# Revit family: COFFRET ELEC HOSPIVAC G EVISA
name_source: partatom
category: Equipement de génie climatique
revit_build: Autodesk Revit 2018 (Build: 20170223_1515(x64)
units: mm (PartAtom-declared; Revit-internal decimal feet)

## family parameters
Basée sur le plan de construction = Non
Classification = Aucun
Cote de connecteur circulaire = Utiliser le diamètre
Couper avec des vides une fois chargée = Non
Partagée = Non
Point de calcul de pièce = Non
Toujours verticalement = Oui
Type d'élément = Normal

## types (33) — shared parameters
BRANCHEMENT_TERRE = Oui
COS_PHI = 0.9
DOUBLE_ALIMENTATION = Oui
EMBASE_IG = 60 mm  [stored 0.19685 ft]
HAUTEUR = 344 mm
HAUT_PE = 22.5 mm  [stored 0.0738189 ft]
HAUT_PM2 = 195 mm  [stored 0.639764 ft]
LONGUEUR = 600 mm  [stored 1.9685 ft]
LONG_COFF = 600 mm  [stored 1.9685 ft]
NBR_POLES = 3
NEUTRE = Oui
PROF_IG = 44 mm  [stored 0.144357 ft]
TENSION_ALIM = 400 V
ZONE_MAINTENANCE = Oui
ØDEPART = 20 mm  [stored 0.0656168 ft]
ØFIX = 12 mm  [stored 0.0393701 ft]
ØPE = 40 mm
zero-valued in all types: POIDS(Kg)

## per-type parameters (varying)
- COFFRET PM2 HOSPIVAC G2 E025.R: DESCR_ALIM_MOT=Puissance moteur ; 4G2.5mm²; DESCR_ALIM_MOT_3=Ne pas utiliser; DESCR_ALIM_MOT_4=Ne pas utiliser; DESCR_ALIM_X=Alimentation X ; 5G2.5mm²; DESCR_ALIM_Y=Alimentation Y ; 5G2.5mm²; ENTRAXE_IG=425 mm  [stored 1.39436 ft]; ENTRAXE_PE=526 mm  [stored 1.72572 ft]; HAUT_COFF=300 mm  [stored 0.984252 ft]; HAUT_FIX=258 mm; LARGEUR=300 mm  [stored 0.984252 ft]; LARG_COFF=300 mm  [stored 0.984252 ft]; LONG_FIX=558 mm; OFFSET_HAUT_IG=107.5 mm; OFFSET_HAUT_PM2=135 mm; OFFSET_LARG_PE=80 mm  [stored 0.262467 ft]; PROTECTION_AMONT_X=Disjoncteur courbe D 10A; PROTECTION_AMONT_Y=Disjoncteur courbe D 10A; PUISS_APPARENTE=833 VA; PUISS_APPARENTE_2=833 VA; PUISS_APPARENTE_MOT=833 VA; PUISS_APPARENTE_MOT_3=0 VA; PUISS_APPARENTE_MOT_4=0 VA; PUISS_ELECT=1 kW; PUISS_ELECT_2=1 kW; PUISS_MOT=1 kW; PUISS_MOT_3=0 kW; PUISS_MOT_4=0 kW
- COFFRET PM2 HOSPIVAC G2 E040.R: DESCR_ALIM_MOT=Puissance moteur ; 4G2.5mm²; DESCR_ALIM_MOT_3=Ne pas utiliser; DESCR_ALIM_MOT_4=Ne pas utiliser; DESCR_ALIM_X=Alimentation X ; 5G2.5mm²; DESCR_ALIM_Y=Alimentation Y ; 5G2.5mm²; ENTRAXE_IG=425 mm  [stored 1.39436 ft]; ENTRAXE_PE=526 mm  [stored 1.72572 ft]; HAUT_COFF=300 mm  [stored 0.984252 ft]; HAUT_FIX=258 mm; LARGEUR=300 mm  [stored 0.984252 ft]; LARG_COFF=300 mm  [stored 0.984252 ft]; LONG_FIX=558 mm; OFFSET_HAUT_IG=107.5 mm; OFFSET_HAUT_PM2=135 mm; OFFSET_LARG_PE=80 mm  [stored 0.262467 ft]; PROTECTION_AMONT_X=Disjoncteur courbe D 10A; PROTECTION_AMONT_Y=Disjoncteur courbe D 10A; PUISS_APPARENTE=1222 VA; PUISS_APPARENTE_2=1222 VA; PUISS_APPARENTE_MOT=1222 VA; PUISS_APPARENTE_MOT_3=0 VA; PUISS_APPARENTE_MOT_4=0 VA; PUISS_ELECT=1 kW; PUISS_ELECT_2=1 kW; PUISS_MOT=1 kW; PUISS_MOT_3=0 kW; PUISS_MOT_4=0 kW
- COFFRET PM2 HOSPIVAC G2 E065.R: DESCR_ALIM_MOT=Puissance moteur ; 4G2.5mm²; DESCR_ALIM_MOT_3=Ne pas utiliser; DESCR_ALIM_MOT_4=Ne pas utiliser; DESCR_ALIM_X=Alimentation X ; 5G2.5mm²; DESCR_ALIM_Y=Alimentation Y ; 5G2.5mm²; ENTRAXE_IG=425 mm  [stored 1.39436 ft]; ENTRAXE_PE=526 mm  [stored 1.72572 ft]; HAUT_COFF=300 mm  [stored 0.984252 ft]; HAUT_FIX=258 mm; LARGEUR=300 mm  [stored 0.984252 ft]; LARG_COFF=300 mm  [stored 0.984252 ft]; LONG_FIX=558 mm; OFFSET_HAUT_IG=107.5 mm; OFFSET_HAUT_PM2=135 mm; OFFSET_LARG_PE=80 mm  [stored 0.262467 ft]; PROTECTION_AMONT_X=Disjoncteur courbe D 10A; PROTECTION_AMONT_Y=Disjoncteur courbe D 10A; PUISS_APPARENTE=1667 VA; PUISS_APPARENTE_2=1667 VA; PUISS_APPARENTE_MOT=1667 VA; PUISS_APPARENTE_MOT_3=0 VA; PUISS_APPARENTE_MOT_4=0 VA; PUISS_ELECT=2 kW; PUISS_ELECT_2=2 kW; PUISS_MOT=2 kW; PUISS_MOT_3=0 kW; PUISS_MOT_4=0 kW
- COFFRET PM2 HOSPIVAC G3 E025.R: DESCR_ALIM_MOT=Puissance moteur ; 4G2.5mm²; DESCR_ALIM_MOT_3=Puissance moteur ; 4G2.5mm²; DESCR_ALIM_MOT_4=Ne pas utiliser; DESCR_ALIM_X=Alimentation X ; 5G2.5mm²; DESCR_ALIM_Y=Alimentation Y ; 5G2.5mm²; ENTRAXE_IG=425 mm  [stored 1.39436 ft]; ENTRAXE_PE=526 mm  [stored 1.72572 ft]; HAUT_COFF=300 mm  [stored 0.984252 ft]; HAUT_FIX=258 mm; LARGEUR=300 mm  [stored 0.984252 ft]; LARG_COFF=300 mm  [stored 0.984252 ft]; LONG_FIX=558 mm; OFFSET_HAUT_IG=107.5 mm; OFFSET_HAUT_PM2=135 mm; OFFSET_LARG_PE=80 mm  [stored 0.262467 ft]; PROTECTION_AMONT_X=Disjoncteur courbe D 6A; PROTECTION_AMONT_Y=Disjoncteur courbe D 10A; PUISS_APPARENTE=833 VA; PUISS_APPARENTE_2=1667 VA; PUISS_APPARENTE_MOT=833 VA; PUISS_APPARENTE_MOT_3=833 VA; PUISS_APPARENTE_MOT_4=0 VA; PUISS_ELECT=1 kW; PUISS_ELECT_2=2 kW; PUISS_MOT=1 kW; PUISS_MOT_3=1 kW; PUISS_MOT_4=0 kW
- COFFRET PM2 HOSPIVAC G3 E040.R: DESCR_ALIM_MOT=Puissance moteur ; 4G2.5mm²; DESCR_ALIM_MOT_3=Puissance moteur ; 4G2.5mm²; DESCR_ALIM_MOT_4=Ne pas utiliser; DESCR_ALIM_X=Alimentation X ; 5G2.5mm²; DESCR_ALIM_Y=Alimentation Y ; 5G2.5mm²; ENTRAXE_IG=425 mm  [stored 1.39436 ft]; ENTRAXE_PE=526 mm  [stored 1.72572 ft]; HAUT_COFF=300 mm  [stored 0.984252 ft]; HAUT_FIX=258 mm; LARGEUR=300 mm  [stored 0.984252 ft]; LARG_COFF=300 mm  [stored 0.984252 ft]; LONG_FIX=558 mm; OFFSET_HAUT_IG=107.5 mm; OFFSET_HAUT_PM2=135 mm; OFFSET_LARG_PE=80 mm  [stored 0.262467 ft]; PROTECTION_AMONT_X=Disjoncteur courbe D 6A; PROTECTION_AMONT_Y=Disjoncteur courbe D 10A; PUISS_APPARENTE=1222 VA; PUISS_APPARENTE_2=2444 VA; PUISS_APPARENTE_MOT=1222 VA; PUISS_APPARENTE_MOT_3=1222 VA; PUISS_APPARENTE_MOT_4=0 VA; PUISS_ELECT=1 kW; PUISS_ELECT_2=2 kW; PUISS_MOT=1 kW; PUISS_MOT_3=1 kW; PUISS_MOT_4=0 kW
- COFFRET PM2 HOSPIVAC G3 E065.R: DESCR_ALIM_MOT=Puissance moteur ; 4G2.5mm²; DESCR_ALIM_MOT_3=Puissance moteur ; 4G2.5mm²; DESCR_ALIM_MOT_4=Ne pas utiliser; DESCR_ALIM_X=Alimentation X ; 5G2.5mm²; DESCR_ALIM_Y=Alimentation Y ; 5G2.5mm²; ENTRAXE_IG=425 mm  [stored 1.39436 ft]; ENTRAXE_PE=526 mm  [stored 1.72572 ft]; HAUT_COFF=300 mm  [stored 0.984252 ft]; HAUT_FIX=258 mm; LARGEUR=300 mm  [stored 0.984252 ft]; LARG_COFF=300 mm  [stored 0.984252 ft]; LONG_FIX=558 mm; OFFSET_HAUT_IG=107.5 mm; OFFSET_HAUT_PM2=135 mm; OFFSET_LARG_PE=80 mm  [stored 0.262467 ft]; PROTECTION_AMONT_X=Disjoncteur courbe D 6A; PROTECTION_AMONT_Y=Disjoncteur courbe D 16A; PUISS_APPARENTE=1667 VA; PUISS_APPARENTE_2=3333 VA; PUISS_APPARENTE_MOT=1667 VA; PUISS_APPARENTE_MOT_3=1667 VA; PUISS_APPARENTE_MOT_4=0 VA; PUISS_ELECT=2 kW; PUISS_ELECT_2=3 kW; PUISS_MOT=2 kW; PUISS_MOT_3=2 kW; PUISS_MOT_4=0 kW
- COFFRET PM2 HOSPIVAC G4 E100.R: DESCR_ALIM_MOT=Puissance moteur ; 4G2.5mm²; DESCR_ALIM_MOT_3=Puissance moteur ; 4G2.5mm²; DESCR_ALIM_MOT_4=Puissance moteur ; 4G2.5mm²; DESCR_ALIM_X=Alimentation X ; 5G2.5mm²; DESCR_ALIM_Y=Alimentation Y ; 5G2.5mm²; ENTRAXE_IG=180 mm  [stored 0.590551 ft]; ENTRAXE_PE=420 mm  [stored 1.37795 ft]; HAUT_COFF=800 mm  [stored 2.62467 ft]; HAUT_FIX=755 mm  [stored 2.47703 ft]; LARGEUR=250 mm  [stored 0.82021 ft]; LARG_COFF=250 mm  [stored 0.82021 ft]; LONG_FIX=555 mm  [stored 1.82087 ft]; OFFSET_HAUT_IG=165 mm; OFFSET_HAUT_PM2=320 mm  [stored 1.04987 ft]; OFFSET_LARG_PE=185 mm  [stored 0.606955 ft]; PROTECTION_AMONT_X=Disjoncteur courbe D 16A; PROTECTION_AMONT_Y=Disjoncteur courbe D 16A; PUISS_APPARENTE=4889 VA; PUISS_APPARENTE_2=4889 VA; PUISS_APPARENTE_MOT=2444 VA; PUISS_APPARENTE_MOT_3=2444 VA; PUISS_APPARENTE_MOT_4=2444 VA; PUISS_ELECT=4 kW; PUISS_ELECT_2=4 kW; PUISS_MOT=2 kW; PUISS_MOT_3=2 kW; PUISS_MOT_4=2 kW
- COFFRET PM2 HOSPIVAC G4 E150.R: DESCR_ALIM_MOT=Puissance moteur ; 4G2.5mm²; DESCR_ALIM_MOT_3=Puissance moteur ; 4G2.5mm²; DESCR_ALIM_MOT_4=Puissance moteur ; 4G2.5mm²; DESCR_ALIM_X=Alimentation X ; 5G4mm²; DESCR_ALIM_Y=Alimentation Y ; 5G4mm²; ENTRAXE_IG=180 mm  [stored 0.590551 ft]; ENTRAXE_PE=420 mm  [stored 1.37795 ft]; HAUT_COFF=800 mm  [stored 2.62467 ft]; HAUT_FIX=755 mm  [stored 2.47703 ft]; LARGEUR=250 mm  [stored 0.82021 ft]; LARG_COFF=250 mm  [stored 0.82021 ft]; LONG_FIX=555 mm  [stored 1.82087 ft]; OFFSET_HAUT_IG=165 mm; OFFSET_HAUT_PM2=320 mm  [stored 1.04987 ft]; OFFSET_LARG_PE=185 mm  [stored 0.606955 ft]; PROTECTION_AMONT_X=Disjoncteur courbe D 20A; PROTECTION_AMONT_Y=Disjoncteur courbe D 20A; PUISS_APPARENTE=6667 VA; PUISS_APPARENTE_2=6667 VA; PUISS_APPARENTE_MOT=3333 VA; PUISS_APPARENTE_MOT_3=3333 VA; PUISS_APPARENTE_MOT_4=3333 VA; PUISS_ELECT=6 kW; PUISS_ELECT_2=6 kW; PUISS_MOT=3 kW; PUISS_MOT_3=3 kW; PUISS_MOT_4=3 kW
- COFFRET PM2 HOSPIVAC G4 E300.R: DESCR_ALIM_MOT=Puissance moteur ; 4G2.5mm²; DESCR_ALIM_MOT_3=Puissance moteur ; 4G2.5mm²; DESCR_ALIM_MOT_4=Puissance moteur ; 4G2.5mm²; DESCR_ALIM_X=Alimentation X ; 5G10mm²; DESCR_ALIM_Y=Alimentation Y ; 5G10mm²; ENTRAXE_IG=180 mm  [stored 0.590551 ft]; ENTRAXE_PE=420 mm  [stored 1.37795 ft]; HAUT_COFF=800 mm  [stored 2.62467 ft]; HAUT_FIX=755 mm  [stored 2.47703 ft]; LARGEUR=250 mm  [stored 0.82021 ft]; LARG_COFF=250 mm  [stored 0.82021 ft]; LONG_FIX=555 mm  [stored 1.82087 ft]; OFFSET_HAUT_IG=165 mm; OFFSET_HAUT_PM2=320 mm  [stored 1.04987 ft]; OFFSET_LARG_PE=185 mm  [stored 0.606955 ft]; PROTECTION_AMONT_X=Disjoncteur courbe D 32A; PROTECTION_AMONT_Y=Disjoncteur courbe D 32A; PUISS_APPARENTE=12222 VA; PUISS_APPARENTE_2=12222 VA; PUISS_APPARENTE_MOT=6111 VA; PUISS_APPARENTE_MOT_3=6111 VA; PUISS_APPARENTE_MOT_4=6111 VA; PUISS_ELECT=11 kW; PUISS_ELECT_2=11 kW; PUISS_MOT=6 kW; PUISS_MOT_3=6 kW; PUISS_MOT_4=6 kW
- COFFRET PM2 HOSPIVAC G2 E100.R: DESCR_ALIM_MOT=Puissance moteur ; 4G2.5mm²; DESCR_ALIM_MOT_3=Ne pas utiliser; DESCR_ALIM_MOT_4=Ne pas utiliser; DESCR_ALIM_X=Alimentation X ; 5G2.5mm²; DESCR_ALIM_Y=Alimentation Y ; 5G2.5mm²; ENTRAXE_IG=425 mm  [stored 1.39436 ft]; ENTRAXE_PE=526 mm  [stored 1.72572 ft]; HAUT_COFF=300 mm  [stored 0.984252 ft]; HAUT_FIX=258 mm; LARGEUR=300 mm  [stored 0.984252 ft]; LARG_COFF=300 mm  [stored 0.984252 ft]; LONG_FIX=558 mm; OFFSET_HAUT_IG=107.5 mm; OFFSET_HAUT_PM2=135 mm; OFFSET_LARG_PE=80 mm  [stored 0.262467 ft]; PROTECTION_AMONT_X=Disjoncteur courbe D 10A; PROTECTION_AMONT_Y=Disjoncteur courbe D 10A; PUISS_APPARENTE=2444 VA; PUISS_APPARENTE_2=2444 VA; PUISS_APPARENTE_MOT=2444 VA; PUISS_APPARENTE_MOT_3=0 VA; PUISS_APPARENTE_MOT_4=0 VA; PUISS_ELECT=2 kW; PUISS_ELECT_2=2 kW; PUISS_MOT=2 kW; PUISS_MOT_3=0 kW; PUISS_MOT_4=0 kW
- COFFRET PM2 HOSPIVAC G2 E150.R: DESCR_ALIM_MOT=Puissance moteur ; 4G2.5mm²; DESCR_ALIM_MOT_3=Ne pas utiliser; DESCR_ALIM_MOT_4=Ne pas utiliser; DESCR_ALIM_X=Alimentation X ; 5G2.5mm²; DESCR_ALIM_Y=Alimentation Y ; 5G2.5mm²; ENTRAXE_IG=425 mm  [stored 1.39436 ft]; ENTRAXE_PE=526 mm  [stored 1.72572 ft]; HAUT_COFF=300 mm  [stored 0.984252 ft]; HAUT_FIX=258 mm; LARGEUR=300 mm  [stored 0.984252 ft]; LARG_COFF=300 mm  [stored 0.984252 ft]; LONG_FIX=558 mm; OFFSET_HAUT_IG=107.5 mm; OFFSET_HAUT_PM2=135 mm; OFFSET_LARG_PE=80 mm  [stored 0.262467 ft]; PROTECTION_AMONT_X=Disjoncteur courbe D 10A; PROTECTION_AMONT_Y=Disjoncteur courbe D 10A; PUISS_APPARENTE=3333 VA; PUISS_APPARENTE_2=3333 VA; PUISS_APPARENTE_MOT=3333 VA; PUISS_APPARENTE_MOT_3=0 VA; PUISS_APPARENTE_MOT_4=0 VA; PUISS_ELECT=3 kW; PUISS_ELECT_2=3 kW; PUISS_MOT=3 kW; PUISS_MOT_3=0 kW; PUISS_MOT_4=0 kW
- COFFRET PM2 HOSPIVAC G2 E200.R: DESCR_ALIM_MOT=Puissance moteur ; 4G2.5mm²; DESCR_ALIM_MOT_3=Ne pas utiliser; DESCR_ALIM_MOT_4=Ne pas utiliser; DESCR_ALIM_X=Alimentation X ; 5G2.5mm²; DESCR_ALIM_Y=Alimentation Y ; 5G2.5mm²; ENTRAXE_IG=425 mm  [stored 1.39436 ft]; ENTRAXE_PE=526 mm  [stored 1.72572 ft]; HAUT_COFF=300 mm  [stored 0.984252 ft]; HAUT_FIX=258 mm; LARGEUR=300 mm  [stored 0.984252 ft]; LARG_COFF=300 mm  [stored 0.984252 ft]; LONG_FIX=558 mm; OFFSET_HAUT_IG=107.5 mm; OFFSET_HAUT_PM2=135 mm; OFFSET_LARG_PE=80 mm  [stored 0.262467 ft]; PROTECTION_AMONT_X=Disjoncteur courbe D 16A; PROTECTION_AMONT_Y=Disjoncteur courbe D 16A; PUISS_APPARENTE=4444 VA; PUISS_APPARENTE_2=4444 VA; PUISS_APPARENTE_MOT=4444 VA; PUISS_APPARENTE_MOT_3=0 VA; PUISS_APPARENTE_MOT_4=0 VA; PUISS_ELECT=4 kW; PUISS_ELECT_2=4 kW; PUISS_MOT=4 kW; PUISS_MOT_3=0 kW; PUISS_MOT_4=0 kW
- COFFRET PM2 HOSPIVAC G2 E300.R: DESCR_ALIM_MOT=Puissance moteur ; 4G2.5mm²; DESCR_ALIM_MOT_3=Ne pas utiliser; DESCR_ALIM_MOT_4=Ne pas utiliser; DESCR_ALIM_X=Alimentation X ; 5G2.5mm²; DESCR_ALIM_Y=Alimentation Y ; 5G2.5mm²; ENTRAXE_IG=425 mm  [stored 1.39436 ft]; ENTRAXE_PE=526 mm  [stored 1.72572 ft]; HAUT_COFF=300 mm  [stored 0.984252 ft]; HAUT_FIX=258 mm; LARGEUR=300 mm  [stored 0.984252 ft]; LARG_COFF=300 mm  [stored 0.984252 ft]; LONG_FIX=558 mm; OFFSET_HAUT_IG=107.5 mm; OFFSET_HAUT_PM2=135 mm; OFFSET_LARG_PE=80 mm  [stored 0.262467 ft]; PROTECTION_AMONT_X=Disjoncteur courbe D 16A; PROTECTION_AMONT_Y=Disjoncteur courbe D 16A; PUISS_APPARENTE=6111 VA; PUISS_APPARENTE_2=6111 VA; PUISS_APPARENTE_MOT=6111 VA; PUISS_APPARENTE_MOT_3=0 VA; PUISS_APPARENTE_MOT_4=0 VA; PUISS_ELECT=6 kW; PUISS_ELECT_2=6 kW; PUISS_MOT=6 kW; PUISS_MOT_3=0 kW; PUISS_MOT_4=0 kW
- COFFRET PM2 HOSPIVAC G2 E350.R: DESCR_ALIM_MOT=Puissance moteur ; 4G4mm²; DESCR_ALIM_MOT_3=Ne pas utiliser; DESCR_ALIM_MOT_4=Ne pas utiliser; DESCR_ALIM_X=Alimentation X ; 5G4mm²; DESCR_ALIM_Y=Alimentation Y ; 5G4mm²; ENTRAXE_IG=425 mm  [stored 1.39436 ft]; ENTRAXE_PE=526 mm  [stored 1.72572 ft]; HAUT_COFF=300 mm  [stored 0.984252 ft]; HAUT_FIX=258 mm; LARGEUR=300 mm  [stored 0.984252 ft]; LARG_COFF=300 mm  [stored 0.984252 ft]; LONG_FIX=558 mm; OFFSET_HAUT_IG=107.5 mm; OFFSET_HAUT_PM2=135 mm; OFFSET_LARG_PE=80 mm  [stored 0.262467 ft]; PROTECTION_AMONT_X=Disjoncteur courbe D 25A; PROTECTION_AMONT_Y=Disjoncteur courbe D 25A; PUISS_APPARENTE=8333 VA; PUISS_APPARENTE_2=8333 VA; PUISS_APPARENTE_MOT=8333 VA; PUISS_APPARENTE_MOT_3=0 VA; PUISS_APPARENTE_MOT_4=0 VA; PUISS_ELECT=8 kW; PUISS_ELECT_2=8 kW; PUISS_MOT=8 kW; PUISS_MOT_3=0 kW; PUISS_MOT_4=0 kW
- COFFRET PM2 HOSPIVAC G2 E400.R: DESCR_ALIM_MOT=Puissance moteur ; 4G6mm²; DESCR_ALIM_MOT_3=Ne pas utiliser; DESCR_ALIM_MOT_4=Ne pas utiliser; DESCR_ALIM_X=Alimentation X ; 5G6mm²; DESCR_ALIM_Y=Alimentation Y ; 5G6mm²; ENTRAXE_IG=425 mm  [stored 1.39436 ft]; ENTRAXE_PE=526 mm  [stored 1.72572 ft]; HAUT_COFF=300 mm  [stored 0.984252 ft]; HAUT_FIX=258 mm; LARGEUR=300 mm  [stored 0.984252 ft]; LARG_COFF=300 mm  [stored 0.984252 ft]; LONG_FIX=558 mm; OFFSET_HAUT_IG=107.5 mm; OFFSET_HAUT_PM2=135 mm; OFFSET_LARG_PE=80 mm  [stored 0.262467 ft]; PROTECTION_AMONT_X=Disjoncteur courbe D 32A; PROTECTION_AMONT_Y=Disjoncteur courbe D 32A; PUISS_APPARENTE=10000 VA; PUISS_APPARENTE_2=10000 VA; PUISS_APPARENTE_MOT=10000 VA; PUISS_APPARENTE_MOT_3=0 VA; PUISS_APPARENTE_MOT_4=0 VA; PUISS_ELECT=9 kW; PUISS_ELECT_2=9 kW; PUISS_MOT=9 kW; PUISS_MOT_3=0 kW; PUISS_MOT_4=0 kW
- COFFRET PM2 HOSPIVAC G2 E500.R: DESCR_ALIM_MOT=Puissance moteur ; 4G6mm²; DESCR_ALIM_MOT_3=Ne pas utiliser; DESCR_ALIM_MOT_4=Ne pas utiliser; DESCR_ALIM_X=Alimentation X ; 5G6mm²; DESCR_ALIM_Y=Alimentation Y ; 5G6mm²; ENTRAXE_IG=425 mm  [stored 1.39436 ft]; ENTRAXE_PE=526 mm  [stored 1.72572 ft]; HAUT_COFF=300 mm  [stored 0.984252 ft]; HAUT_FIX=258 mm; LARGEUR=300 mm  [stored 0.984252 ft]; LARG_COFF=300 mm  [stored 0.984252 ft]; LONG_FIX=558 mm; OFFSET_HAUT_IG=107.5 mm; OFFSET_HAUT_PM2=135 mm; OFFSET_LARG_PE=80 mm  [stored 0.262467 ft]; PROTECTION_AMONT_X=Disjoncteur courbe D 32A; PROTECTION_AMONT_Y=Disjoncteur courbe D 32A; PUISS_APPARENTE=12222 VA; PUISS_APPARENTE_2=12222 VA; PUISS_APPARENTE_MOT=12222 VA; PUISS_APPARENTE_MOT_3=0 VA; PUISS_APPARENTE_MOT_4=0 VA; PUISS_ELECT=11 kW; PUISS_ELECT_2=11 kW; PUISS_MOT=11 kW; PUISS_MOT_3=0 kW; PUISS_MOT_4=0 kW
- COFFRET PM2 HOSPIVAC G2 E600.R: DESCR_ALIM_MOT=Puissance moteur ; 4G10mm²; DESCR_ALIM_MOT_3=Ne pas utiliser; DESCR_ALIM_MOT_4=Ne pas utiliser; DESCR_ALIM_X=Alimentation X ; 5G10mm²; DESCR_ALIM_Y=Alimentation Y ; 5G10mm²; ENTRAXE_IG=425 mm  [stored 1.39436 ft]; ENTRAXE_PE=526 mm  [stored 1.72572 ft]; HAUT_COFF=300 mm  [stored 0.984252 ft]; HAUT_FIX=258 mm; LARGEUR=300 mm  [stored 0.984252 ft]; LARG_COFF=300 mm  [stored 0.984252 ft]; LONG_FIX=558 mm; OFFSET_HAUT_IG=107.5 mm; OFFSET_HAUT_PM2=135 mm; OFFSET_LARG_PE=80 mm  [stored 0.262467 ft]; PROTECTION_AMONT_X=Disjoncteur courbe D 40A; PROTECTION_AMONT_Y=Disjoncteur courbe D 40A; PUISS_APPARENTE=16667 VA; PUISS_APPARENTE_2=16667 VA; PUISS_APPARENTE_MOT=16667 VA; PUISS_APPARENTE_MOT_3=0 VA; PUISS_APPARENTE_MOT_4=0 VA; PUISS_ELECT=15 kW; PUISS_ELECT_2=15 kW; PUISS_MOT=15 kW; PUISS_MOT_3=0 kW; PUISS_MOT_4=0 kW
- COFFRET PM2 HOSPIVAC G3 E100.R: DESCR_ALIM_MOT=Puissance moteur ; 4G2.5mm²; DESCR_ALIM_MOT_3=Puissance moteur ; 4G2.5mm²; DESCR_ALIM_MOT_4=Ne pas utiliser; DESCR_ALIM_X=Alimentation X ; 5G2.5mm²; DESCR_ALIM_Y=Alimentation Y ; 5G2.5mm²; ENTRAXE_IG=425 mm  [stored 1.39436 ft]; ENTRAXE_PE=526 mm  [stored 1.72572 ft]; HAUT_COFF=300 mm  [stored 0.984252 ft]; HAUT_FIX=258 mm; LARGEUR=300 mm  [stored 0.984252 ft]; LARG_COFF=300 mm  [stored 0.984252 ft]; LONG_FIX=558 mm; OFFSET_HAUT_IG=107.5 mm; OFFSET_HAUT_PM2=135 mm; OFFSET_LARG_PE=80 mm  [stored 0.262467 ft]; PROTECTION_AMONT_X=Disjoncteur courbe D 10A; PROTECTION_AMONT_Y=Disjoncteur courbe D 16A; PUISS_APPARENTE=2444 VA; PUISS_APPARENTE_2=4889 VA; PUISS_APPARENTE_MOT=2444 VA; PUISS_APPARENTE_MOT_3=2444 VA; PUISS_APPARENTE_MOT_4=0 VA; PUISS_ELECT=2 kW; PUISS_ELECT_2=4 kW; PUISS_MOT=2 kW; PUISS_MOT_3=2 kW; PUISS_MOT_4=0 kW
- COFFRET PM2 HOSPIVAC G3 E150.R: DESCR_ALIM_MOT=Puissance moteur ; 4G2.5mm²; DESCR_ALIM_MOT_3=Puissance moteur ; 4G2.5mm²; DESCR_ALIM_MOT_4=Ne pas utiliser; DESCR_ALIM_X=Alimentation X ; 5G2.5mm²; DESCR_ALIM_Y=Alimentation Y ; 5G4mm²; ENTRAXE_IG=425 mm  [stored 1.39436 ft]; ENTRAXE_PE=526 mm  [stored 1.72572 ft]; HAUT_COFF=300 mm  [stored 0.984252 ft]; HAUT_FIX=258 mm; LARGEUR=300 mm  [stored 0.984252 ft]; LARG_COFF=300 mm  [stored 0.984252 ft]; LONG_FIX=558 mm; OFFSET_HAUT_IG=107.5 mm; OFFSET_HAUT_PM2=135 mm; OFFSET_LARG_PE=80 mm  [stored 0.262467 ft]; PROTECTION_AMONT_X=Disjoncteur courbe D 10A; PROTECTION_AMONT_Y=Disjoncteur courbe D 20A; PUISS_APPARENTE=3333 VA; PUISS_APPARENTE_2=6667 VA; PUISS_APPARENTE_MOT=3333 VA; PUISS_APPARENTE_MOT_3=3333 VA; PUISS_APPARENTE_MOT_4=0 VA; PUISS_ELECT=3 kW; PUISS_ELECT_2=6 kW; PUISS_MOT=3 kW; PUISS_MOT_3=3 kW; PUISS_MOT_4=0 kW
- COFFRET PM2 HOSPIVAC G3 E200.R: DESCR_ALIM_MOT=Puissance moteur ; 4G2.5mm²; DESCR_ALIM_MOT_3=Puissance moteur ; 4G2.5mm²; DESCR_ALIM_MOT_4=Ne pas utiliser; DESCR_ALIM_X=Alimentation X ; 5G2.5mm²; DESCR_ALIM_Y=Alimentation Y ; 5G6mm²; ENTRAXE_IG=425 mm  [stored 1.39436 ft]; ENTRAXE_PE=526 mm  [stored 1.72572 ft]; HAUT_COFF=300 mm  [stored 0.984252 ft]; HAUT_FIX=258 mm; LARGEUR=300 mm  [stored 0.984252 ft]; LARG_COFF=300 mm  [stored 0.984252 ft]; LONG_FIX=558 mm; OFFSET_HAUT_IG=107.5 mm; OFFSET_HAUT_PM2=135 mm; OFFSET_LARG_PE=80 mm  [stored 0.262467 ft]; PROTECTION_AMONT_X=Disjoncteur courbe D 16A; PROTECTION_AMONT_Y=Disjoncteur courbe D 25A; PUISS_APPARENTE=4444 VA; PUISS_APPARENTE_2=8889 VA; PUISS_APPARENTE_MOT=4444 VA; PUISS_APPARENTE_MOT_3=4444 VA; PUISS_APPARENTE_MOT_4=0 VA; PUISS_ELECT=4 kW; PUISS_ELECT_2=8 kW; PUISS_MOT=4 kW; PUISS_MOT_3=4 kW; PUISS_MOT_4=0 kW
- COFFRET PM2 HOSPIVAC G3 E300.R: DESCR_ALIM_MOT=Puissance moteur ; 4G2.5mm²; DESCR_ALIM_MOT_3=Puissance moteur ; 4G2.5mm²; DESCR_ALIM_MOT_4=Ne pas utiliser; DESCR_ALIM_X=Alimentation X ; 5G2.5mm²; DESCR_ALIM_Y=Alimentation Y ; 5G10mm²; ENTRAXE_IG=425 mm  [stored 1.39436 ft]; ENTRAXE_PE=526 mm  [stored 1.72572 ft]; HAUT_COFF=300 mm  [stored 0.984252 ft]; HAUT_FIX=258 mm; LARGEUR=300 mm  [stored 0.984252 ft]; LARG_COFF=300 mm  [stored 0.984252 ft]; LONG_FIX=558 mm; OFFSET_HAUT_IG=107.5 mm; OFFSET_HAUT_PM2=135 mm; OFFSET_LARG_PE=80 mm  [stored 0.262467 ft]; PROTECTION_AMONT_X=Disjoncteur courbe D 16A; PROTECTION_AMONT_Y=Disjoncteur courbe D 32A; PUISS_APPARENTE=6111 VA; PUISS_APPARENTE_2=12222 VA; PUISS_APPARENTE_MOT=6111 VA; PUISS_APPARENTE_MOT_3=6111 VA; PUISS_APPARENTE_MOT_4=0 VA; PUISS_ELECT=6 kW; PUISS_ELECT_2=11 kW; PUISS_MOT=6 kW; PUISS_MOT_3=6 kW; PUISS_MOT_4=0 kW
- COFFRET PM2 HOSPIVAC G3 E350.R: DESCR_ALIM_MOT=Puissance moteur ; 4G4mm²; DESCR_ALIM_MOT_3=Puissance moteur ; 4G4mm²; DESCR_ALIM_MOT_4=Ne pas utiliser; DESCR_ALIM_X=Alimentation X ; 5G4mm²; DESCR_ALIM_Y=Alimentation Y ; 5G16mm²; ENTRAXE_IG=425 mm  [stored 1.39436 ft]; ENTRAXE_PE=526 mm  [stored 1.72572 ft]; HAUT_COFF=300 mm  [stored 0.984252 ft]; HAUT_FIX=258 mm; LARGEUR=300 mm  [stored 0.984252 ft]; LARG_COFF=300 mm  [stored 0.984252 ft]; LONG_FIX=558 mm; OFFSET_HAUT_IG=107.5 mm; OFFSET_HAUT_PM2=135 mm; OFFSET_LARG_PE=80 mm  [stored 0.262467 ft]; PROTECTION_AMONT_X=Disjoncteur courbe D 25A; PROTECTION_AMONT_Y=Disjoncteur courbe D 50A; PUISS_APPARENTE=8333 VA; PUISS_APPARENTE_2=16667 VA; PUISS_APPARENTE_MOT=8333 VA; PUISS_APPARENTE_MOT_3=8333 VA; PUISS_APPARENTE_MOT_4=0 VA; PUISS_ELECT=8 kW; PUISS_ELECT_2=15 kW; PUISS_MOT=8 kW; PUISS_MOT_3=8 kW; PUISS_MOT_4=0 kW
- COFFRET PM2 HOSPIVAC G3 E400.R: DESCR_ALIM_MOT=Puissance moteur ; 4G6mm²; DESCR_ALIM_MOT_3=Puissance moteur ; 4G6mm²; DESCR_ALIM_MOT_4=Ne pas utiliser; DESCR_ALIM_X=Alimentation X ; 5G6mm²; DESCR_ALIM_Y=Alimentation Y ; 5G16mm²; ENTRAXE_IG=425 mm  [stored 1.39436 ft]; ENTRAXE_PE=526 mm  [stored 1.72572 ft]; HAUT_COFF=300 mm  [stored 0.984252 ft]; HAUT_FIX=258 mm; LARGEUR=300 mm  [stored 0.984252 ft]; LARG_COFF=300 mm  [stored 0.984252 ft]; LONG_FIX=558 mm; OFFSET_HAUT_IG=107.5 mm; OFFSET_HAUT_PM2=135 mm; OFFSET_LARG_PE=80 mm  [stored 0.262467 ft]; PROTECTION_AMONT_X=Disjoncteur courbe D 32A; PROTECTION_AMONT_Y=Disjoncteur courbe D 63A; PUISS_APPARENTE=10000 VA; PUISS_APPARENTE_2=20000 VA; PUISS_APPARENTE_MOT=10000 VA; PUISS_APPARENTE_MOT_3=10000 VA; PUISS_APPARENTE_MOT_4=0 VA; PUISS_ELECT=9 kW; PUISS_ELECT_2=18 kW; PUISS_MOT=9 kW; PUISS_MOT_3=9 kW; PUISS_MOT_4=0 kW
- COFFRET PM2 HOSPIVAC G3 E500.R: DESCR_ALIM_MOT=Puissance moteur ; 4G6mm²; DESCR_ALIM_MOT_3=Puissance moteur ; 4G6mm²; DESCR_ALIM_MOT_4=Ne pas utiliser; DESCR_ALIM_X=Alimentation X ; 5G6mm²; DESCR_ALIM_Y=Alimentation Y ; 2x5G6mm²; ENTRAXE_IG=425 mm  [stored 1.39436 ft]; ENTRAXE_PE=526 mm  [stored 1.72572 ft]; HAUT_COFF=300 mm  [stored 0.984252 ft]; HAUT_FIX=258 mm; LARGEUR=300 mm  [stored 0.984252 ft]; LARG_COFF=300 mm  [stored 0.984252 ft]; LONG_FIX=558 mm; OFFSET_HAUT_IG=107.5 mm; OFFSET_HAUT_PM2=135 mm; OFFSET_LARG_PE=80 mm  [stored 0.262467 ft]; PROTECTION_AMONT_X=Disjoncteur courbe D 32A; PROTECTION_AMONT_Y=Disjoncteur courbe D 63A; PUISS_APPARENTE=12222 VA; PUISS_APPARENTE_2=24444 VA; PUISS_APPARENTE_MOT=12222 VA; PUISS_APPARENTE_MOT_3=12222 VA; PUISS_APPARENTE_MOT_4=0 VA; PUISS_ELECT=11 kW; PUISS_ELECT_2=22 kW; PUISS_MOT=11 kW; PUISS_MOT_3=11 kW; PUISS_MOT_4=0 kW
- COFFRET PM2 HOSPIVAC G3 E600.R: DESCR_ALIM_MOT=Puissance moteur ; 4G10mm²; DESCR_ALIM_MOT_3=Puissance moteur ; 4G10mm²; DESCR_ALIM_MOT_4=Ne pas utiliser; DESCR_ALIM_X=Alimentation X ; 5G10mm²; DESCR_ALIM_Y=Alimentation Y ; 2x5G10mm²; ENTRAXE_IG=425 mm  [stored 1.39436 ft]; ENTRAXE_PE=526 mm  [stored 1.72572 ft]; HAUT_COFF=300 mm  [stored 0.984252 ft]; HAUT_FIX=258 mm; LARGEUR=300 mm  [stored 0.984252 ft]; LARG_COFF=300 mm  [stored 0.984252 ft]; LONG_FIX=558 mm; OFFSET_HAUT_IG=107.5 mm; OFFSET_HAUT_PM2=135 mm; OFFSET_LARG_PE=80 mm  [stored 0.262467 ft]; PROTECTION_AMONT_X=Disjoncteur courbe D 40A; PROTECTION_AMONT_Y=Disjoncteur courbe D 80A; PUISS_APPARENTE=16667 VA; PUISS_APPARENTE_2=33333 VA; PUISS_APPARENTE_MOT=16667 VA; PUISS_APPARENTE_MOT_3=16667 VA; PUISS_APPARENTE_MOT_4=0 VA; PUISS_ELECT=15 kW; PUISS_ELECT_2=30 kW; PUISS_MOT=15 kW; PUISS_MOT_3=15 kW; PUISS_MOT_4=0 kW
- COFFRET PM2 HOSPIVAC G4 E025.R: DESCR_ALIM_MOT=Puissance moteur ; 4G2.5mm²; DESCR_ALIM_MOT_3=Puissance moteur ; 4G2.5mm²; DESCR_ALIM_MOT_4=Puissance moteur ; 4G2.5mm²; DESCR_ALIM_X=Alimentation X ; 5G2.5mm²; DESCR_ALIM_Y=Alimentation Y ; 5G2.5mm²; ENTRAXE_IG=180 mm  [stored 0.590551 ft]; ENTRAXE_PE=420 mm  [stored 1.37795 ft]; HAUT_COFF=800 mm  [stored 2.62467 ft]; HAUT_FIX=755 mm  [stored 2.47703 ft]; LARGEUR=250 mm  [stored 0.82021 ft]; LARG_COFF=250 mm  [stored 0.82021 ft]; LONG_FIX=555 mm  [stored 1.82087 ft]; OFFSET_HAUT_IG=165 mm; OFFSET_HAUT_PM2=320 mm  [stored 1.04987 ft]; OFFSET_LARG_PE=185 mm  [stored 0.606955 ft]; PROTECTION_AMONT_X=Disjoncteur courbe D 10A; PROTECTION_AMONT_Y=Disjoncteur courbe D 10A; PUISS_APPARENTE=1667 VA; PUISS_APPARENTE_2=1667 VA; PUISS_APPARENTE_MOT=833 VA; PUISS_APPARENTE_MOT_3=833 VA; PUISS_APPARENTE_MOT_4=833 VA; PUISS_ELECT=2 kW; PUISS_ELECT_2=2 kW; PUISS_MOT=1 kW; PUISS_MOT_3=1 kW; PUISS_MOT_4=1 kW
- COFFRET PM2 HOSPIVAC G4 E040.R: DESCR_ALIM_MOT=Puissance moteur ; 4G2.5mm²; DESCR_ALIM_MOT_3=Puissance moteur ; 4G2.5mm²; DESCR_ALIM_MOT_4=Puissance moteur ; 4G2.5mm²; DESCR_ALIM_X=Alimentation X ; 5G2.5mm²; DESCR_ALIM_Y=Alimentation Y ; 5G2.5mm²; ENTRAXE_IG=180 mm  [stored 0.590551 ft]; ENTRAXE_PE=420 mm  [stored 1.37795 ft]; HAUT_COFF=800 mm  [stored 2.62467 ft]; HAUT_FIX=755 mm  [stored 2.47703 ft]; LARGEUR=250 mm  [stored 0.82021 ft]; LARG_COFF=250 mm  [stored 0.82021 ft]; LONG_FIX=555 mm  [stored 1.82087 ft]; OFFSET_HAUT_IG=165 mm; OFFSET_HAUT_PM2=320 mm  [stored 1.04987 ft]; OFFSET_LARG_PE=185 mm  [stored 0.606955 ft]; PROTECTION_AMONT_X=Disjoncteur courbe D 10A; PROTECTION_AMONT_Y=Disjoncteur courbe D 10A; PUISS_APPARENTE=2444 VA; PUISS_APPARENTE_2=2444 VA; PUISS_APPARENTE_MOT=1222 VA; PUISS_APPARENTE_MOT_3=1222 VA; PUISS_APPARENTE_MOT_4=1222 VA; PUISS_ELECT=2 kW; PUISS_ELECT_2=2 kW; PUISS_MOT=1 kW; PUISS_MOT_3=1 kW; PUISS_MOT_4=1 kW
- COFFRET PM2 HOSPIVAC G4 E065.R: DESCR_ALIM_MOT=Puissance moteur ; 4G2.5mm²; DESCR_ALIM_MOT_3=Puissance moteur ; 4G2.5mm²; DESCR_ALIM_MOT_4=Puissance moteur ; 4G2.5mm²; DESCR_ALIM_X=Alimentation X ; 5G2.5mm²; DESCR_ALIM_Y=Alimentation Y ; 5G2.5mm²; ENTRAXE_IG=180 mm  [stored 0.590551 ft]; ENTRAXE_PE=420 mm  [stored 1.37795 ft]; HAUT_COFF=800 mm  [stored 2.62467 ft]; HAUT_FIX=755 mm  [stored 2.47703 ft]; LARGEUR=250 mm  [stored 0.82021 ft]; LARG_COFF=250 mm  [stored 0.82021 ft]; LONG_FIX=555 mm  [stored 1.82087 ft]; OFFSET_HAUT_IG=165 mm; OFFSET_HAUT_PM2=320 mm  [stored 1.04987 ft]; OFFSET_LARG_PE=185 mm  [stored 0.606955 ft]; PROTECTION_AMONT_X=Disjoncteur courbe D 16A; PROTECTION_AMONT_Y=Disjoncteur courbe D 16A; PUISS_APPARENTE=3333 VA; PUISS_APPARENTE_2=3333 VA; PUISS_APPARENTE_MOT=1667 VA; PUISS_APPARENTE_MOT_3=1667 VA; PUISS_APPARENTE_MOT_4=1667 VA; PUISS_ELECT=3 kW; PUISS_ELECT_2=3 kW; PUISS_MOT=2 kW; PUISS_MOT_3=2 kW; PUISS_MOT_4=2 kW
- COFFRET PM2 HOSPIVAC G4 E200.R: DESCR_ALIM_MOT=Puissance moteur ; 4G2.5mm²; DESCR_ALIM_MOT_3=Puissance moteur ; 4G2.5mm²; DESCR_ALIM_MOT_4=Puissance moteur ; 4G2.5mm²; DESCR_ALIM_X=Alimentation X ; 5G6mm²; DESCR_ALIM_Y=Alimentation Y ; 5G6mm²; ENTRAXE_IG=180 mm  [stored 0.590551 ft]; ENTRAXE_PE=420 mm  [stored 1.37795 ft]; HAUT_COFF=800 mm  [stored 2.62467 ft]; HAUT_FIX=755 mm  [stored 2.47703 ft]; LARGEUR=250 mm  [stored 0.82021 ft]; LARG_COFF=250 mm  [stored 0.82021 ft]; LONG_FIX=555 mm  [stored 1.82087 ft]; OFFSET_HAUT_IG=165 mm; OFFSET_HAUT_PM2=320 mm  [stored 1.04987 ft]; OFFSET_LARG_PE=185 mm  [stored 0.606955 ft]; PROTECTION_AMONT_X=Disjoncteur courbe D 25A; PROTECTION_AMONT_Y=Disjoncteur courbe D 25A; PUISS_APPARENTE=8889 VA; PUISS_APPARENTE_2=8889 VA; PUISS_APPARENTE_MOT=4444 VA; PUISS_APPARENTE_MOT_3=4444 VA; PUISS_APPARENTE_MOT_4=4444 VA; PUISS_ELECT=8 kW; PUISS_ELECT_2=8 kW; PUISS_MOT=4 kW; PUISS_MOT_3=4 kW; PUISS_MOT_4=4 kW
- COFFRET PM2 HOSPIVAC G4 E400.R: DESCR_ALIM_MOT=Puissance moteur ; 4G6mm²; DESCR_ALIM_MOT_3=Puissance moteur ; 4G6mm²; DESCR_ALIM_MOT_4=Puissance moteur ; 4G6mm²; DESCR_ALIM_X=Alimentation X ; 5G16mm²; DESCR_ALIM_Y=Alimentation Y ; 5G16mm²; ENTRAXE_IG=180 mm  [stored 0.590551 ft]; ENTRAXE_PE=420 mm  [stored 1.37795 ft]; HAUT_COFF=800 mm  [stored 2.62467 ft]; HAUT_FIX=755 mm  [stored 2.47703 ft]; LARGEUR=250 mm  [stored 0.82021 ft]; LARG_COFF=250 mm  [stored 0.82021 ft]; LONG_FIX=555 mm  [stored 1.82087 ft]; OFFSET_HAUT_IG=165 mm; OFFSET_HAUT_PM2=320 mm  [stored 1.04987 ft]; OFFSET_LARG_PE=185 mm  [stored 0.606955 ft]; PROTECTION_AMONT_X=Disjoncteur courbe D 63A; PROTECTION_AMONT_Y=Disjoncteur courbe D 63A; PUISS_APPARENTE=20000 VA; PUISS_APPARENTE_2=20000 VA; PUISS_APPARENTE_MOT=10000 VA; PUISS_APPARENTE_MOT_3=10000 VA; PUISS_APPARENTE_MOT_4=10000 VA; PUISS_ELECT=18 kW; PUISS_ELECT_2=18 kW; PUISS_MOT=9 kW; PUISS_MOT_3=9 kW; PUISS_MOT_4=9 kW
- COFFRET PM2 HOSPIVAC G4 E350.R: DESCR_ALIM_MOT=Puissance moteur ; 4G4mm²; DESCR_ALIM_MOT_3=Puissance moteur ; 4G4mm²; DESCR_ALIM_MOT_4=Puissance moteur ; 4G4mm²; DESCR_ALIM_X=Alimentation X ; 5G16mm²; DESCR_ALIM_Y=Alimentation Y ; 5G16mm²; ENTRAXE_IG=180 mm  [stored 0.590551 ft]; ENTRAXE_PE=420 mm  [stored 1.37795 ft]; HAUT_COFF=800 mm  [stored 2.62467 ft]; HAUT_FIX=755 mm  [stored 2.47703 ft]; LARGEUR=250 mm  [stored 0.82021 ft]; LARG_COFF=250 mm  [stored 0.82021 ft]; LONG_FIX=555 mm  [stored 1.82087 ft]; OFFSET_HAUT_IG=165 mm; OFFSET_HAUT_PM2=320 mm  [stored 1.04987 ft]; OFFSET_LARG_PE=185 mm  [stored 0.606955 ft]; PROTECTION_AMONT_X=Disjoncteur courbe D 50A; PROTECTION_AMONT_Y=Disjoncteur courbe D 50A; PUISS_APPARENTE=16667 VA; PUISS_APPARENTE_2=16667 VA; PUISS_APPARENTE_MOT=8333 VA; PUISS_APPARENTE_MOT_3=8333 VA; PUISS_APPARENTE_MOT_4=8333 VA; PUISS_ELECT=15 kW; PUISS_ELECT_2=15 kW; PUISS_MOT=8 kW; PUISS_MOT_3=8 kW; PUISS_MOT_4=8 kW
- COFFRET PM2 HOSPIVAC G4 E500.R: DESCR_ALIM_MOT=Puissance moteur ; 4G6mm²; DESCR_ALIM_MOT_3=Puissance moteur ; 4G6mm²; DESCR_ALIM_MOT_4=Puissance moteur ; 4G6mm²; DESCR_ALIM_X=Alimentation X ; 2x5G6mm²; DESCR_ALIM_Y=Alimentation Y ; 2x5G6mm²; ENTRAXE_IG=180 mm  [stored 0.590551 ft]; ENTRAXE_PE=420 mm  [stored 1.37795 ft]; HAUT_COFF=800 mm  [stored 2.62467 ft]; HAUT_FIX=755 mm  [stored 2.47703 ft]; LARGEUR=250 mm  [stored 0.82021 ft]; LARG_COFF=250 mm  [stored 0.82021 ft]; LONG_FIX=555 mm  [stored 1.82087 ft]; OFFSET_HAUT_IG=165 mm; OFFSET_HAUT_PM2=320 mm  [stored 1.04987 ft]; OFFSET_LARG_PE=185 mm  [stored 0.606955 ft]; PROTECTION_AMONT_X=Disjoncteur courbe D 63A; PROTECTION_AMONT_Y=Disjoncteur courbe D 63A; PUISS_APPARENTE=24444 VA; PUISS_APPARENTE_2=24444 VA; PUISS_APPARENTE_MOT=12222 VA; PUISS_APPARENTE_MOT_3=12222 VA; PUISS_APPARENTE_MOT_4=12222 VA; PUISS_ELECT=22 kW; PUISS_ELECT_2=22 kW; PUISS_MOT=11 kW; PUISS_MOT_3=11 kW; PUISS_MOT_4=11 kW
- COFFRET PM2 HOSPIVAC G4 E600.R: DESCR_ALIM_MOT=Puissance moteur ; 4G10mm²; DESCR_ALIM_MOT_3=Puissance moteur ; 4G10mm²; DESCR_ALIM_MOT_4=Puissance moteur ; 4G10mm²; DESCR_ALIM_X=Alimentation X ; 2x5G10mm²; DESCR_ALIM_Y=Alimentation Y ; 2x5G10mm²; ENTRAXE_IG=180 mm  [stored 0.590551 ft]; ENTRAXE_PE=420 mm  [stored 1.37795 ft]; HAUT_COFF=800 mm  [stored 2.62467 ft]; HAUT_FIX=755 mm  [stored 2.47703 ft]; LARGEUR=250 mm  [stored 0.82021 ft]; LARG_COFF=250 mm  [stored 0.82021 ft]; LONG_FIX=555 mm  [stored 1.82087 ft]; OFFSET_HAUT_IG=165 mm; OFFSET_HAUT_PM2=320 mm  [stored 1.04987 ft]; OFFSET_LARG_PE=185 mm  [stored 0.606955 ft]; PROTECTION_AMONT_X=Disjoncteur courbe D 80A; PROTECTION_AMONT_Y=Disjoncteur courbe D 80A; PUISS_APPARENTE=33333 VA; PUISS_APPARENTE_2=33333 VA; PUISS_APPARENTE_MOT=16667 VA; PUISS_APPARENTE_MOT_3=16667 VA; PUISS_APPARENTE_MOT_4=16667 VA; PUISS_ELECT=30 kW; PUISS_ELECT_2=30 kW; PUISS_MOT=15 kW; PUISS_MOT_3=15 kW; PUISS_MOT_4=15 kW

note: [stored X ft] marks values corroborated as IEEE doubles in the binary element streams (Revit-internal decimal feet)
